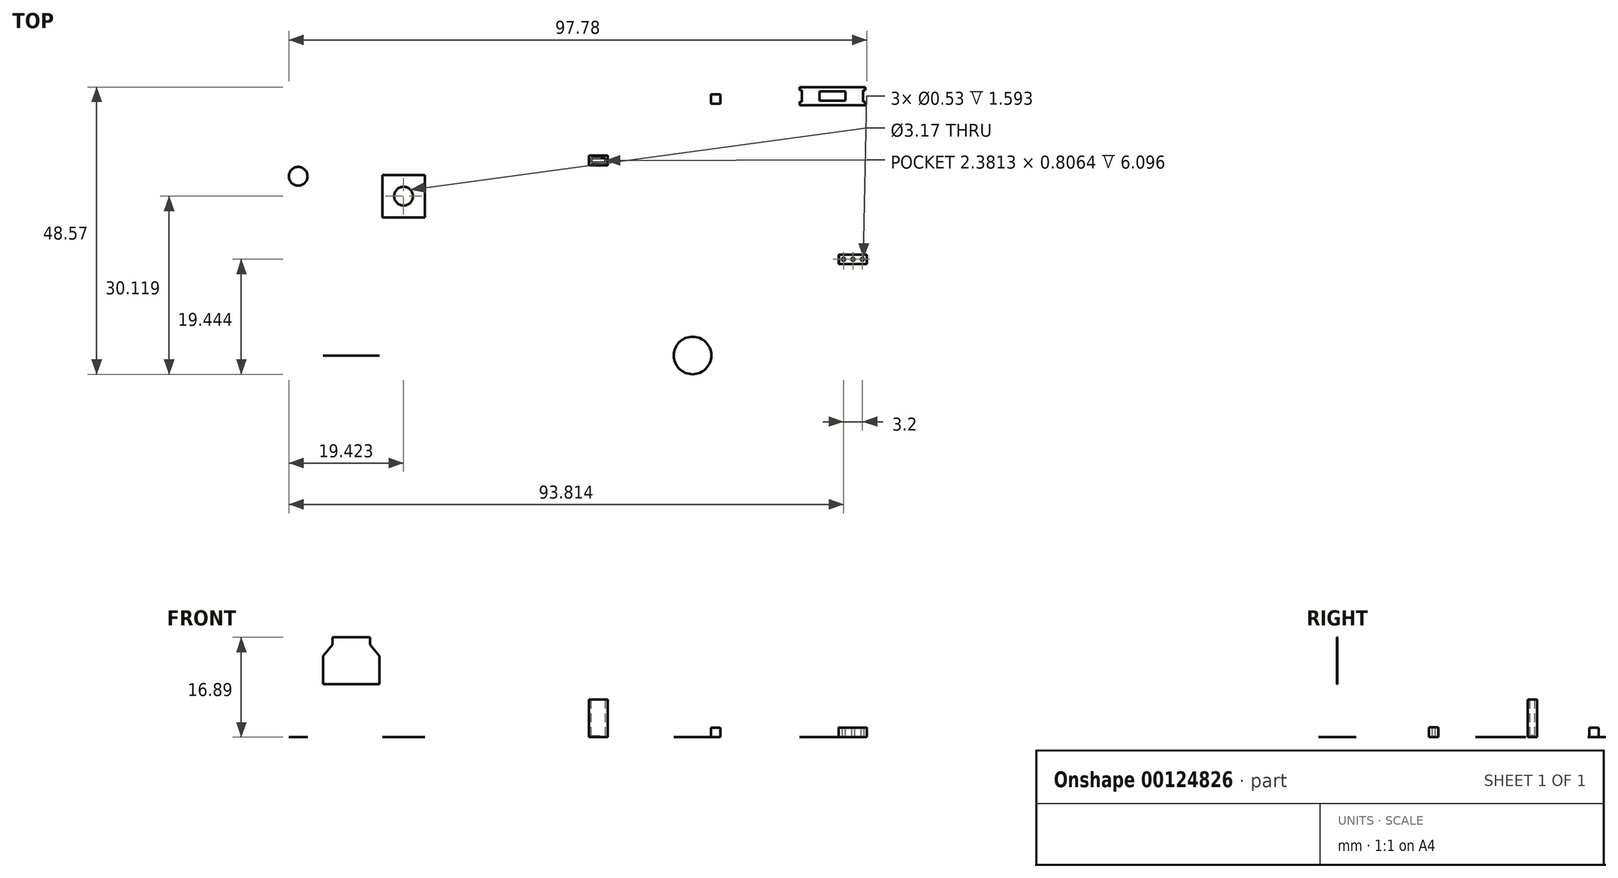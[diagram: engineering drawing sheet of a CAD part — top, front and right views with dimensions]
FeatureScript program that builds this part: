
annotation { "Feature Type Name" : "Feature", "Feature Type Description" : "" }
export const myFeature = defineFeature(function(context is Context, id is Id, definition is map)
    precondition{}
    {
        {
            var Q0;
            Q0=qCreatedBy(makeId("Top.planeOp"),FACE);
            var sketch = newSketch(context, id + "F0", { "sketchPlane" : qUnion([Q0])});
            skCircle(sketch, "E0", {"center": v(0, 0) * mm, "radius": 3.18 * mm});
            skSolve(sketch);
        }
        {
            var Q0;
            Q0=makeQuery(id+"F0.imprint","IMPRINT",FACE,{"disambiguationData":[TD([[makeQuery(id+"F0.imprint","IMPRINT",EDGE,{"derivedFrom":sQuery(id+"F0.wireOp",EDGE,"E0")}),1.0]])]});
            extrude(context, id + "F1", {"entities" : qUnion([Q0]), "depth" : 9 / 812.8 * mm});
        }
        {
            var Q0;
            Q0=qCreatedBy(makeId("Front.planeOp"),FACE);
            var sketch = newSketch(context, id + "F2", { "sketchPlane" : qUnion([Q0])});
            skLineSegment(sketch, "E1", {"start": v(-62.48, 13.74) * mm, "end": v(-62.48, 8.98) * mm});
            skLineSegment(sketch, "E2", {"start": v(-62.48, 8.98) * mm, "end": v(-52.95, 8.98) * mm});
            skLineSegment(sketch, "E3", {"start": v(-52.95, 8.98) * mm, "end": v(-52.95, 13.74) * mm});
            skLineSegment(sketch, "E4", {"start": v(-52.95, 13.74) * mm, "end": v(-54.54, 15.63) * mm});
            skLineSegment(sketch, "E5", {"start": v(-54.54, 15.63) * mm, "end": v(-54.54, 16.9) * mm});
            skLineSegment(sketch, "E6", {"start": v(-62.48, 13.74) * mm, "end": v(-60.9, 15.63) * mm});
            skLineSegment(sketch, "E7", {"start": v(-60.9, 15.63) * mm, "end": v(-60.9, 16.9) * mm});
            skLineSegment(sketch, "E8", {"start": v(-60.9, 16.9) * mm, "end": v(-54.54, 16.9) * mm});
            skLineSegment(sketch, "E9", {"start": v(-62.48, 13.74) * mm, "end": v(-62.48, 16.9) * mm});
            skLineSegment(sketch, "E10", {"start": v(-62.48, 16.9) * mm, "end": v(-60.9, 16.9) * mm});
            skLineSegment(sketch, "E11", {"start": v(-52.95, 13.74) * mm, "end": v(-52.95, 16.9) * mm});
            skLineSegment(sketch, "E12", {"start": v(-54.54, 16.9) * mm, "end": v(-52.95, 16.9) * mm});
            skSolve(sketch);
        }
        {
            var Q0;
            Q0=makeQuery(id+"F2.imprint","IMPRINT",FACE,{"disambiguationData":[TD([[makeQuery(id+"F2.imprint","IMPRINT",EDGE,{"derivedFrom":sQuery(id+"F2.wireOp",EDGE,"E1")}),1.0]])]});
            extrude(context, id + "F3", {"entities" : qUnion([Q0]), "depth" : 11 / 203.2 * mm});
        }
        {
            var Q0;
            Q0=qCreatedBy(makeId("Top.planeOp"),FACE);
            var sketch = newSketch(context, id + "F4", { "sketchPlane" : qUnion([Q0])});
            skLineSegment(sketch, "E13.bottom", {"start": v(-52.43, 30.51) * mm, "end": v(-45.29, 30.51) * mm});
            skLineSegment(sketch, "E13.top", {"start": v(-52.43, 23.37) * mm, "end": v(-45.29, 23.37) * mm});
            skLineSegment(sketch, "E13.left", {"start": v(-52.43, 30.51) * mm, "end": v(-52.43, 23.37) * mm});
            skLineSegment(sketch, "E13.right", {"start": v(-45.29, 30.51) * mm, "end": v(-45.29, 23.37) * mm});
            skCircle(sketch, "E14", {"center": v(-48.86, 26.94) * mm, "radius": 1.59 * mm});
            skPoint(sketch, "E14.centerSnap0", {"position": v(-52.43, 26.94) * mm});
            skPoint(sketch, "E14.centerSnap1", {"position": v(-48.86, 30.51) * mm});
            skCircle(sketch, "E15", {"center": v(-46.08, 29.72) * mm, "radius": 0.4 * mm});
            skCircle(sketch, "E16.1.0", {"center": v(-51.64, 29.72) * mm, "radius": 0.4 * mm});
            skCircle(sketch, "E16.2.0", {"center": v(-51.64, 24.16) * mm, "radius": 0.4 * mm});
            skCircle(sketch, "E16.3.0", {"center": v(-46.08, 24.16) * mm, "radius": 0.4 * mm});
            skSolve(sketch);
        }
        {
            var Q0;
            Q0=makeQuery(id+"F4.imprint","IMPRINT",FACE,{"disambiguationData":[TD([[makeQuery(id+"F4.imprint","IMPRINT",EDGE,{"derivedFrom":sQuery(id+"F4.wireOp",EDGE,"E13.bottom")}),-1.0]])]});
            extrude(context, id + "F5", {"entities" : qUnion([Q0]), "depth" : 3 / 406.4 * mm});
        }
        {
            var Q0;
            Q0=makeQuery(id+"F4.imprint","IMPRINT",FACE,{"disambiguationData":[TD([[makeQuery(id+"F4.imprint","IMPRINT",EDGE,{"derivedFrom":sQuery(id+"F4.wireOp",EDGE,"E16.1.0")}),1.0]])]});
            var Q1;
            Q1=makeQuery(id+"F4.imprint","IMPRINT",FACE,{"disambiguationData":[TD([[makeQuery(id+"F4.imprint","IMPRINT",EDGE,{"derivedFrom":sQuery(id+"F4.wireOp",EDGE,"E15")}),1.0]])]});
            var Q2;
            Q2=makeQuery(id+"F4.imprint","IMPRINT",FACE,{"disambiguationData":[TD([[makeQuery(id+"F4.imprint","IMPRINT",EDGE,{"derivedFrom":sQuery(id+"F4.wireOp",EDGE,"E16.3.0")}),1.0]])]});
            var Q3;
            Q3=makeQuery(id+"F4.imprint","IMPRINT",FACE,{"disambiguationData":[TD([[makeQuery(id+"F4.imprint","IMPRINT",EDGE,{"derivedFrom":sQuery(id+"F4.wireOp",EDGE,"E16.2.0")}),1.0]])]});
            extrude(context, id + "F6", {"entities" : qUnion([Q0, Q1, Q2, Q3]), "operationType" : NewBodyOperationType.ADD, "depth" : 13 / 1625.6 * mm});
        }
        {
            var Q0;
            Q0=qCreatedBy(makeId("Top.planeOp"),FACE);
            var sketch = newSketch(context, id + "F7", { "sketchPlane" : qUnion([Q0])});
            skLineSegment(sketch, "E17", {"start": v(18.1, 45.39) * mm, "end": v(29.21, 45.39) * mm});
            skLineSegment(sketch, "E18", {"start": v(29.21, 45.39) * mm, "end": v(29.21, 44.86) * mm});
            skLineSegment(sketch, "E19", {"start": v(29.21, 44.86) * mm, "end": v(28.82, 44.86) * mm});
            skLineSegment(sketch, "E20", {"start": v(28.82, 44.86) * mm, "end": v(28.82, 42.87) * mm});
            skLineSegment(sketch, "E21", {"start": v(29.21, 42.87) * mm, "end": v(28.82, 42.87) * mm});
            skLineSegment(sketch, "E22", {"start": v(29.21, 42.87) * mm, "end": v(29.21, 42.34) * mm});
            skLineSegment(sketch, "E23", {"start": v(29.21, 42.34) * mm, "end": v(18.1, 42.34) * mm});
            skLineSegment(sketch, "E24", {"start": v(18.1, 42.34) * mm, "end": v(18.1, 42.87) * mm});
            skLineSegment(sketch, "E25", {"start": v(18.1, 42.87) * mm, "end": v(18.5, 42.87) * mm});
            skPoint(sketch, "E25.endSnap0", {"position": v(29.02, 42.87) * mm});
            skLineSegment(sketch, "E26", {"start": v(18.5, 42.87) * mm, "end": v(18.5, 44.86) * mm});
            skLineSegment(sketch, "E27", {"start": v(18.5, 44.86) * mm, "end": v(18.1, 44.86) * mm});
            skLineSegment(sketch, "E28", {"start": v(18.1, 44.86) * mm, "end": v(18.1, 45.39) * mm});
            skSolve(sketch);
        }
        {
            var Q0;
            Q0=qSketchRegion(id+"F7",true);
            extrude(context, id + "F8", {"entities" : qUnion([Q0]), "depth" : 3 / 406.4 * mm});
        }
        {
            var Q0;
            Q0=makeQuery(id+"F8.opExtrude","CAP_FACE",FACE,{"disambiguationData":[OSD([sQuery(id+"F7.wireOp",EDGE,"E17"),sQuery(id+"F7.wireOp",EDGE,"E18"),sQuery(id+"F7.wireOp",EDGE,"E19"),sQuery(id+"F7.wireOp",EDGE,"E20"),sQuery(id+"F7.wireOp",EDGE,"E21"),sQuery(id+"F7.wireOp",EDGE,"E22"),sQuery(id+"F7.wireOp",EDGE,"E23"),sQuery(id+"F7.wireOp",EDGE,"E24"),sQuery(id+"F7.wireOp",EDGE,"E25"),sQuery(id+"F7.wireOp",EDGE,"E26"),sQuery(id+"F7.wireOp",EDGE,"E27"),sQuery(id+"F7.wireOp",EDGE,"E28")])],"isStart":false});
            var sketch = newSketch(context, id + "F9", { "sketchPlane" : qUnion([Q0])});
            skLineSegment(sketch, "E29.bottom", {"start": v(21.47, 44.67) * mm, "end": v(25.84, 44.67) * mm});
            skLineSegment(sketch, "E29.top", {"start": v(21.47, 43.07) * mm, "end": v(25.84, 43.07) * mm});
            skLineSegment(sketch, "E29.left", {"start": v(21.47, 44.67) * mm, "end": v(21.47, 43.07) * mm});
            skLineSegment(sketch, "E29.right", {"start": v(25.84, 44.67) * mm, "end": v(25.84, 43.07) * mm});
            skPoint(sketch, "E29.middle", {"position": v(23.66, 43.87) * mm});
            skPoint(sketch, "E29.middle.positionSnap0", {"position": v(18.5, 43.87) * mm});
            skPoint(sketch, "E29.middle.positionSnap1", {"position": v(23.66, 45.39) * mm});
            skPoint(sketch, "E29.centerSnap0", {"position": v(18.5, 43.87) * mm});
            skPoint(sketch, "E29.centerSnap1", {"position": v(23.66, 45.39) * mm});
            skSolve(sketch);
        }
        {
            var Q0;
            Q0=qSketchRegion(id+"F9",true);
            extrude(context, id + "F10", {"entities" : qUnion([Q0]), "operationType" : NewBodyOperationType.REMOVE, "oppositeDirection" : true, "depth" : 1 / 1625.6 * mm});
        }
        {
            var Q0;
            Q0=qCreatedBy(makeId("Top.planeOp"),FACE);
            var sketch = newSketch(context, id + "F11", { "sketchPlane" : qUnion([Q0])});
            skLineSegment(sketch, "E30.bottom", {"start": v(4.73, 42.6) * mm, "end": v(3.14, 42.6) * mm});
            skLineSegment(sketch, "E30.top", {"start": v(4.73, 44.18) * mm, "end": v(3.14, 44.18) * mm});
            skLineSegment(sketch, "E30.left", {"start": v(4.73, 42.6) * mm, "end": v(4.73, 44.18) * mm});
            skLineSegment(sketch, "E30.right", {"start": v(3.14, 42.6) * mm, "end": v(3.14, 44.18) * mm});
            skPoint(sketch, "E30.middle", {"position": v(3.93, 43.39) * mm});
            skSolve(sketch);
        }
        {
            var Q0;
            Q0=qSketchRegion(id+"F11",true);
            extrude(context, id + "F12", {"entities" : qUnion([Q0]), "depth" : 1.6 * mm});
        }
        {
            var Q0;
            Q0=qCreatedBy(makeId("Top.planeOp"),FACE);
            var sketch = newSketch(context, id + "F13", { "sketchPlane" : qUnion([Q0])});
            skLineSegment(sketch, "E31.bottom", {"start": v(29.5, 15.46) * mm, "end": v(24.74, 15.46) * mm});
            skLineSegment(sketch, "E31.top", {"start": v(29.5, 17.06) * mm, "end": v(24.74, 17.06) * mm});
            skLineSegment(sketch, "E31.left", {"start": v(29.5, 15.46) * mm, "end": v(29.5, 17.06) * mm});
            skLineSegment(sketch, "E31.right", {"start": v(24.74, 15.46) * mm, "end": v(24.74, 17.06) * mm});
            skPoint(sketch, "E31.middle", {"position": v(27.12, 16.26) * mm});
            skCircle(sketch, "E32", {"center": v(25.53, 16.26) * mm, "radius": 0.26 * mm});
            skPoint(sketch, "E32.centerSnap0", {"position": v(24.74, 16.26) * mm});
            skCircle(sketch, "E33.1.0.0", {"center": v(27.13, 16.26) * mm, "radius": 0.26 * mm});
            skCircle(sketch, "E33.2.0.0", {"center": v(28.73, 16.26) * mm, "radius": 0.26 * mm});
            skLineSegment(sketch, "E33.direction1", {"start": v(25.53, 16.26) * mm, "end": v(27.13, 16.26) * mm, "construction": true});
            skSolve(sketch);
        }
        {
            var Q0;
            Q0=makeQuery(id+"F13.imprint","IMPRINT",FACE,{"disambiguationData":[TD([[makeQuery(id+"F13.imprint","IMPRINT",EDGE,{"derivedFrom":sQuery(id+"F13.wireOp",EDGE,"E31.bottom")}),-1.0]])]});
            extrude(context, id + "F14", {"entities" : qUnion([Q0]), "depth" : 1.6 * mm});
        }
        {
            var Q0;
            Q0=makeQuery(id+"F13.imprint","IMPRINT",FACE,{"disambiguationData":[TD([[makeQuery(id+"F13.imprint","IMPRINT",EDGE,{"derivedFrom":sQuery(id+"F13.wireOp",EDGE,"E32")}),1.0]])]});
            var Q1;
            Q1=makeQuery(id+"F13.imprint","IMPRINT",FACE,{"disambiguationData":[TD([[makeQuery(id+"F13.imprint","IMPRINT",EDGE,{"derivedFrom":sQuery(id+"F13.wireOp",EDGE,"E33.1.0.0")}),1.0]])]});
            var Q2;
            Q2=makeQuery(id+"F13.imprint","IMPRINT",FACE,{"disambiguationData":[TD([[makeQuery(id+"F13.imprint","IMPRINT",EDGE,{"derivedFrom":sQuery(id+"F13.wireOp",EDGE,"E33.2.0.0")}),1.0]])]});
            extrude(context, id + "F15", {"entities" : qUnion([Q0, Q1, Q2]), "operationType" : NewBodyOperationType.ADD, "depth" : 3 / 406.4 * mm});
        }
        {
            var Q0;
            Q0=qCreatedBy(makeId("Top.planeOp"),FACE);
            var sketch = newSketch(context, id + "F16", { "sketchPlane" : qUnion([Q0])});
            skLineSegment(sketch, "E34.bottom", {"start": v(-14.35, 32.2) * mm, "end": v(-17.52, 32.2) * mm});
            skLineSegment(sketch, "E34.top", {"start": v(-14.35, 33.8) * mm, "end": v(-17.52, 33.8) * mm});
            skLineSegment(sketch, "E34.left", {"start": v(-14.35, 32.2) * mm, "end": v(-14.35, 33.8) * mm});
            skLineSegment(sketch, "E34.right", {"start": v(-17.52, 32.2) * mm, "end": v(-17.52, 33.8) * mm});
            skPoint(sketch, "E34.middle", {"position": v(-15.93, 33) * mm});
            skSolve(sketch);
        }
        {
            var Q0;
            Q0=qSketchRegion(id+"F16",true);
            extrude(context, id + "F17", {"entities" : qUnion([Q0]), "depth" : 6.35 * mm});
        }
        {
            var Q0;
            Q0=makeQuery(id+"F17.opExtrude","CAP_FACE",FACE,{"disambiguationData":[OSD([sQuery(id+"F16.wireOp",EDGE,"E34.bottom"),sQuery(id+"F16.wireOp",EDGE,"E34.top"),sQuery(id+"F16.wireOp",EDGE,"E34.left"),sQuery(id+"F16.wireOp",EDGE,"E34.right")])],"isStart":false});
            var sketch = newSketch(context, id + "F18", { "sketchPlane" : qUnion([Q0])});
            skLineSegment(sketch, "E35.bottom", {"start": v(-17.12, 33.4) * mm, "end": v(-14.74, 33.4) * mm});
            skLineSegment(sketch, "E35.top", {"start": v(-17.12, 32.59) * mm, "end": v(-14.74, 32.59) * mm});
            skLineSegment(sketch, "E35.left", {"start": v(-17.12, 33.4) * mm, "end": v(-17.12, 32.59) * mm});
            skLineSegment(sketch, "E35.right", {"start": v(-14.74, 33.4) * mm, "end": v(-14.74, 32.59) * mm});
            skPoint(sketch, "E35.middle", {"position": v(-15.93, 33) * mm});
            skPoint(sketch, "E35.middle.positionSnap0", {"position": v(-17.52, 33) * mm});
            skPoint(sketch, "E35.middle.positionSnap1", {"position": v(-15.93, 33.8) * mm});
            skPoint(sketch, "E35.centerSnap0", {"position": v(-17.52, 33) * mm});
            skPoint(sketch, "E35.centerSnap1", {"position": v(-15.93, 33.8) * mm});
            skSolve(sketch);
        }
        {
            var Q0;
            Q0=qSketchRegion(id+"F18",true);
            extrude(context, id + "F19", {"entities" : qUnion([Q0]), "operationType" : NewBodyOperationType.REMOVE, "oppositeDirection" : true, "depth" : 6.1 * mm});
        }
        {
            var Q0;
            Q0=makeQuery(id+"F14.opExtrude","CAP_FACE",FACE,{"disambiguationData":[OSD([sQuery(id+"F13.wireOp",EDGE,"E31.bottom"),sQuery(id+"F13.wireOp",EDGE,"E31.top"),sQuery(id+"F13.wireOp",EDGE,"E31.left"),sQuery(id+"F13.wireOp",EDGE,"E31.right"),sQuery(id+"F13.wireOp",EDGE,"E32"),sQuery(id+"F13.wireOp",EDGE,"E33.1.0.0"),sQuery(id+"F13.wireOp",EDGE,"E33.2.0.0")])],"isStart":false});
            var sketch = newSketch(context, id + "F20", { "sketchPlane" : qUnion([Q0])});
            skLineSegment(sketch, "E36.bottom", {"start": v(24.74, 17.06) * mm, "end": v(24.8, 17.06) * mm});
            skLineSegment(sketch, "E36.top", {"start": v(24.74, 15.46) * mm, "end": v(24.8, 15.46) * mm});
            skLineSegment(sketch, "E36.left", {"start": v(24.74, 17.06) * mm, "end": v(24.74, 15.46) * mm});
            skLineSegment(sketch, "E36.right", {"start": v(24.8, 17.06) * mm, "end": v(24.8, 15.46) * mm});
            skLineSegment(sketch, "E37.bottom", {"start": v(29.5, 15.46) * mm, "end": v(29.45, 15.46) * mm});
            skLineSegment(sketch, "E37.top", {"start": v(29.5, 17.06) * mm, "end": v(29.45, 17.06) * mm});
            skLineSegment(sketch, "E37.left", {"start": v(29.5, 15.46) * mm, "end": v(29.5, 17.06) * mm});
            skLineSegment(sketch, "E37.right", {"start": v(29.45, 15.46) * mm, "end": v(29.45, 17.06) * mm});
            skSolve(sketch);
        }
        {
            var Q0;
            Q0=qSketchRegion(id+"F20",true);
            extrude(context, id + "F21", {"entities" : qUnion([Q0]), "operationType" : NewBodyOperationType.ADD, "depth" : 0.05 * mm});
        }
        {
            var Q0;
            Q0=qCreatedBy(makeId("Top.planeOp"),FACE);
            var sketch = newSketch(context, id + "F22", { "sketchPlane" : qUnion([Q0])});
            skCircle(sketch, "E38", {"center": v(-66.69, 30.3) * mm, "radius": 1.59 * mm});
            skSolve(sketch);
        }
        {
            var Q0;
            Q0=makeQuery(id+"F22.imprint","IMPRINT",FACE,{"disambiguationData":[TD([[makeQuery(id+"F22.imprint","IMPRINT",EDGE,{"derivedFrom":sQuery(id+"F22.wireOp",EDGE,"E38")}),1.0]])]});
            extrude(context, id + "F23", {"entities" : qUnion([Q0]), "depth" : 1 / 812.8 * mm});
        }
    });
